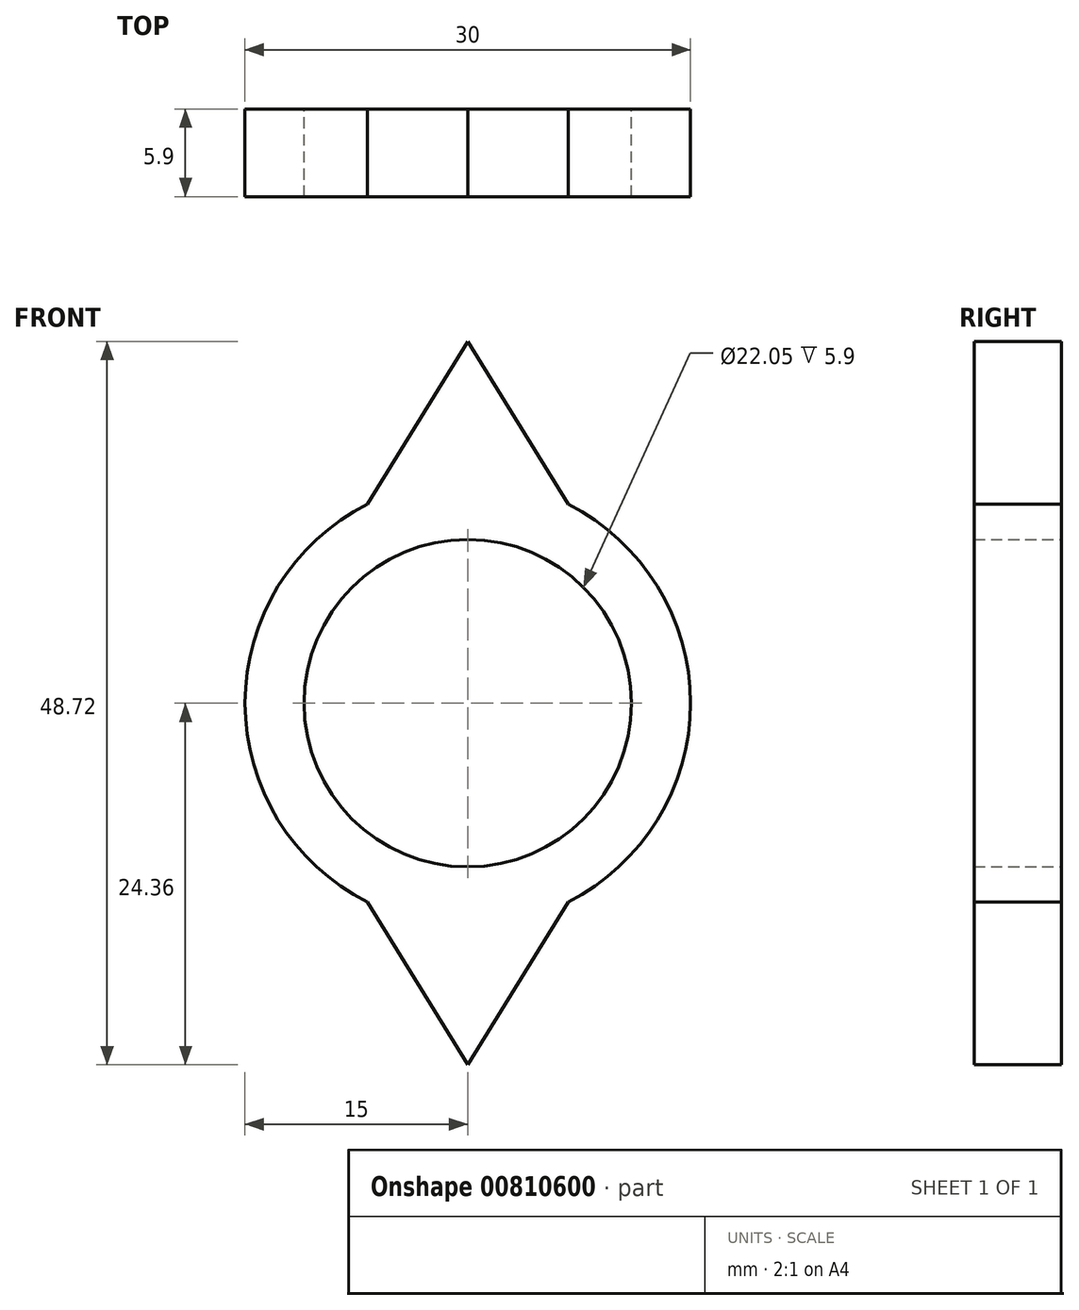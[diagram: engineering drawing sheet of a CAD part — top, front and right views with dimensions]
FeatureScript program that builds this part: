
annotation { "Feature Type Name" : "Feature", "Feature Type Description" : "" }
export const myFeature = defineFeature(function(context is Context, id is Id, definition is map)
    precondition{}
    {
        {
            var Q0;
            Q0=qCreatedBy(makeId("Front.planeOp"),FACE);
            var sketch = newSketch(context, id + "F0", { "sketchPlane" : qUnion([Q0])});
            skCircle(sketch, "E0", {"center": v(0, 0) * mm, "radius": 11.03 * mm});
            skCircle(sketch, "E1", {"center": v(0, 0) * mm, "radius": 15 * mm});
            skSolve(sketch);
        }
        {
            var Q0;
            Q0=qCreatedBy(makeId("Front.planeOp"),FACE);
            var sketch = newSketch(context, id + "F1", { "sketchPlane" : qUnion([Q0])});
            skLineSegment(sketch, "E2", {"start": v(-6.82, 13.29) * mm, "end": v(0, 24.36) * mm});
            skLineSegment(sketch, "E3", {"start": v(0, 24.36) * mm, "end": v(6.82, 13.29) * mm});
            skLineSegment(sketch, "E4", {"start": v(-6.82, -10.49) * mm, "end": v(-6.82, -10.46) * mm});
            skLineSegment(sketch, "E5.left", {"start": v(6.82, 13.29) * mm, "end": v(6.82, 13.29) * mm});
            skLineSegment(sketch, "E5.right", {"start": v(-6.82, 13.29) * mm, "end": v(-6.82, 13.29) * mm});
            skLineSegment(sketch, "E6.top", {"start": v(-6.82, 0) * mm, "end": v(0, 0) * mm});
            skLineSegment(sketch, "E6.left", {"start": v(-6.82, 13.29) * mm, "end": v(-6.82, 0) * mm});
            skLineSegment(sketch, "E7.top", {"start": v(6.82, 0) * mm, "end": v(0, 0) * mm});
            skLineSegment(sketch, "E7.left", {"start": v(6.82, 13.29) * mm, "end": v(6.82, 0) * mm});
            skPoint(sketch, "E8.end.orphan", {"position": v(0, 13.29) * mm});
            skPoint(sketch, "E9.end.orphan", {"position": v(0, -13.36) * mm});
            skPoint(sketch, "E10.end.orphan", {"position": v(-6.82, -13.36) * mm});
            skPoint(sketch, "E11.end.orphan", {"position": v(0, -24.43) * mm});
            skLineSegment(sketch, "E12.MirrorCS", {"start": v(-6.82, -13.29) * mm, "end": v(-6.82, 0) * mm});
            skLineSegment(sketch, "E13.MirrorCS", {"start": v(-6.82, -13.29) * mm, "end": v(0, -24.36) * mm});
            skLineSegment(sketch, "E14.MirrorCS", {"start": v(0, -24.36) * mm, "end": v(6.82, -13.29) * mm});
            skLineSegment(sketch, "E15.MirrorCS", {"start": v(6.82, -13.29) * mm, "end": v(6.82, 0) * mm});
            skSolve(sketch);
        }
        {
            var Q0;
            Q0=makeQuery(id+"F0.imprint","IMPRINT",FACE,{"disambiguationData":[TD([[makeQuery(id+"F0.imprint","IMPRINT",EDGE,{"derivedFrom":sQuery(id+"F0.wireOp",EDGE,"E0")}),-1.0]])]});
            var sketch = newSketch(context, id + "F2", { "sketchPlane" : qUnion([Q0])});
            skSolve(sketch);
        }
        {
            var Q0;
            Q0 = qSketchRegion(id + "F2", true);
            var Q1;
            Q1=makeQuery(id+"F0.imprint","IMPRINT",FACE,{"disambiguationData":[TD([[makeQuery(id+"F0.imprint","IMPRINT",EDGE,{"derivedFrom":sQuery(id+"F0.wireOp",EDGE,"E0")}),-1.0]])]});
            var Q2;
            Q2=makeQuery(id+"F1.imprint","IMPRINT",FACE,{"disambiguationData":[TD([[makeQuery(id+"F1.imprint","IMPRINT",EDGE,{"derivedFrom":sQuery(id+"F1.wireOp",EDGE,"E2")}),-1.0]])]});
            var Q3;
            {var subQ1=sQuery(id+"F1.wireOp",EDGE,"E6.top");Q3=makeQuery(id+"F1.imprint","IMPRINT",FACE,{"disambiguationData":[TD([[makeQuery(id+"F1.imprint","IMPRINT",EDGE,{"derivedFrom":subQ1}),-1.0]])]});}
            extrude(context, id + "F3", {"entities" : qUnion([Q0, Q1, Q2, Q3]), "depth" : 25 * mm, "offsetDistance" : 25 * mm});
        }
        {
            var Q0;
            Q0=makeQuery(id+"F2.imprint","IMPRINT",FACE,{"disambiguationData":[TD([[makeQuery(id+"F2.imprint","IMPRINT",EDGE,{"derivedFrom":makeQuery(id+"F0.imprint","IMPRINT",EDGE,{"derivedFrom":sQuery(id+"F0.wireOp",EDGE,"E0")})}),1.0]])]});
            extrude(context, id + "F4", {"entities" : qUnion([Q0]), "operationType" : NewBodyOperationType.REMOVE, "depth" : 40.1 * mm, "offsetDistance" : 25 * mm});
        }
        {
            var Q0;
            Q0=makeQuery(id+"F4.boolean.opBoolean","SPLIT",BODY,{"disambiguationData":[OD(0.0)],"derivedFrom":makeQuery(id+"F3.opExtrude","SWEPT_BODY",BODY,{"disambiguationData":[OSD([sQuery(id+"F1.wireOp",EDGE,"E2"),sQuery(id+"F1.wireOp",EDGE,"E3"),sQuery(id+"F1.wireOp",EDGE,"E6.left"),sQuery(id+"F1.wireOp",EDGE,"E7.left"),sQuery(id+"F1.wireOp",EDGE,"E12.MirrorCS"),sQuery(id+"F1.wireOp",EDGE,"E13.MirrorCS"),sQuery(id+"F1.wireOp",EDGE,"E14.MirrorCS"),sQuery(id+"F1.wireOp",EDGE,"E15.MirrorCS")])]})});
            var Q1;
            Q1=makeQuery(id+"F3.opExtrude","SWEPT_BODY",BODY,{"disambiguationData":[OSD([sQuery(id+"F0.wireOp",EDGE,"E0"),sQuery(id+"F0.wireOp",EDGE,"E1")])]});
            var Q2;
            Q2=makeQuery(id+"F4.boolean.opBoolean","SPLIT",BODY,{"disambiguationData":[OD(1.0)],"derivedFrom":makeQuery(id+"F3.opExtrude","SWEPT_BODY",BODY,{"disambiguationData":[OSD([sQuery(id+"F1.wireOp",EDGE,"E2"),sQuery(id+"F1.wireOp",EDGE,"E3"),sQuery(id+"F1.wireOp",EDGE,"E6.left"),sQuery(id+"F1.wireOp",EDGE,"E7.left"),sQuery(id+"F1.wireOp",EDGE,"E12.MirrorCS"),sQuery(id+"F1.wireOp",EDGE,"E13.MirrorCS"),sQuery(id+"F1.wireOp",EDGE,"E14.MirrorCS"),sQuery(id+"F1.wireOp",EDGE,"E15.MirrorCS")])]})});
            booleanBodies(context, id + "F5", {"operationType" : BooleanOperationType.UNION, "tools" : qUnion([Q0, Q1, Q2])});
        }
        {
            var Q0;
            {var subQ0=sQuery(id+"F1.wireOp",EDGE,"E14.MirrorCS");var subQ1=sQuery(id+"F1.wireOp",EDGE,"E13.MirrorCS");var subQ2=sQuery(id+"F1.wireOp",EDGE,"E15.MirrorCS");var subQ3=sQuery(id+"F1.wireOp",EDGE,"E7.left");var subQ5=sQuery(id+"F1.wireOp",EDGE,"E12.MirrorCS");var subQ6=sQuery(id+"F1.wireOp",EDGE,"E6.left");var subQ8=sQuery(id+"F0.wireOp",EDGE,"E0");var subQ10=sQuery(id+"F1.wireOp",EDGE,"E3");var subQ11=sQuery(id+"F1.wireOp",EDGE,"E2");var subQ12=makeQuery(id+"F3.opExtrude","CAP_FACE",FACE,{"disambiguationData":[OSD([subQ11,subQ10,subQ6,subQ3,subQ5,subQ1,subQ0,subQ2])],"isStart":false});Q0=makeQuery(id+"F5.opBoolean","MERGE",FACE,{"derivedFrom":[makeQuery(id+"F3.opExtrude","CAP_FACE",FACE,{"disambiguationData":[OSD([subQ8,sQuery(id+"F0.wireOp",EDGE,"E1")])],"isStart":false}),makeQuery(id+"F4.boolean.opBoolean","SPLIT",FACE,{"disambiguationData":[TD([makeQuery(id+"F3.opExtrude","SWEPT_FACE",FACE,{"disambiguationData":[OSD([subQ11])]})])],"derivedFrom":subQ12}),makeQuery(id+"F4.boolean.opBoolean","SPLIT",FACE,{"disambiguationData":[TD([makeQuery(id+"F3.opExtrude","SWEPT_FACE",FACE,{"disambiguationData":[OSD([subQ1])]})])],"derivedFrom":subQ12})]});}
            extrude(context, id + "F6", {"entities" : qUnion([Q0]), "operationType" : NewBodyOperationType.REMOVE, "oppositeDirection" : true, "depth" : 15 * mm, "offsetDistance" : 25 * mm});
        }
        {
            var Q0;
            {var subQ0=sQuery(id+"F1.wireOp",EDGE,"E14.MirrorCS");var subQ1=sQuery(id+"F1.wireOp",EDGE,"E13.MirrorCS");var subQ2=sQuery(id+"F1.wireOp",EDGE,"E15.MirrorCS");var subQ3=sQuery(id+"F1.wireOp",EDGE,"E7.left");var subQ5=sQuery(id+"F1.wireOp",EDGE,"E12.MirrorCS");var subQ6=sQuery(id+"F1.wireOp",EDGE,"E6.left");var subQ8=sQuery(id+"F0.wireOp",EDGE,"E0");var subQ10=sQuery(id+"F1.wireOp",EDGE,"E3");var subQ11=sQuery(id+"F1.wireOp",EDGE,"E2");var subQ12=makeQuery(id+"F3.opExtrude","CAP_FACE",FACE,{"disambiguationData":[OSD([subQ11,subQ10,subQ6,subQ3,subQ5,subQ1,subQ0,subQ2])],"isStart":true});Q0=makeQuery(id+"F5.opBoolean","MERGE",FACE,{"derivedFrom":[makeQuery(id+"F3.opExtrude","CAP_FACE",FACE,{"disambiguationData":[OSD([subQ8,sQuery(id+"F0.wireOp",EDGE,"E1")])],"isStart":true}),makeQuery(id+"F4.boolean.opBoolean","SPLIT",FACE,{"disambiguationData":[TD([makeQuery(id+"F3.opExtrude","SWEPT_FACE",FACE,{"disambiguationData":[OSD([subQ11])]})])],"derivedFrom":subQ12}),makeQuery(id+"F4.boolean.opBoolean","SPLIT",FACE,{"disambiguationData":[TD([makeQuery(id+"F3.opExtrude","SWEPT_FACE",FACE,{"disambiguationData":[OSD([subQ1])]})])],"derivedFrom":subQ12})]});}
            extrude(context, id + "F7", {"entities" : qUnion([Q0]), "operationType" : NewBodyOperationType.REMOVE, "oppositeDirection" : true, "depth" : 7 * mm, "offsetDistance" : 25 * mm});
        }
        {
            var Q0;
            Q0=makeQuery(id+"F6.boolean.opBoolean","COPY",FACE,{"derivedFrom":makeQuery(id+"F6.opExtrude","CAP_FACE",FACE,{"disambiguationData":[OSD([sQuery(id+"F0.wireOp",EDGE,"E0"),sQuery(id+"F0.wireOp",EDGE,"E1"),sQuery(id+"F1.wireOp",EDGE,"E2"),sQuery(id+"F1.wireOp",EDGE,"E3"),sQuery(id+"F1.wireOp",EDGE,"E6.left"),sQuery(id+"F1.wireOp",EDGE,"E7.left"),sQuery(id+"F1.wireOp",EDGE,"E12.MirrorCS"),sQuery(id+"F1.wireOp",EDGE,"E13.MirrorCS"),sQuery(id+"F1.wireOp",EDGE,"E14.MirrorCS"),sQuery(id+"F1.wireOp",EDGE,"E15.MirrorCS")])],"isStart":false})});
            extrude(context, id + "F8", {"entities" : qUnion([Q0]), "operationType" : NewBodyOperationType.ADD, "depth" : 2.9 * mm, "offsetDistance" : 25 * mm});
        }
    });
